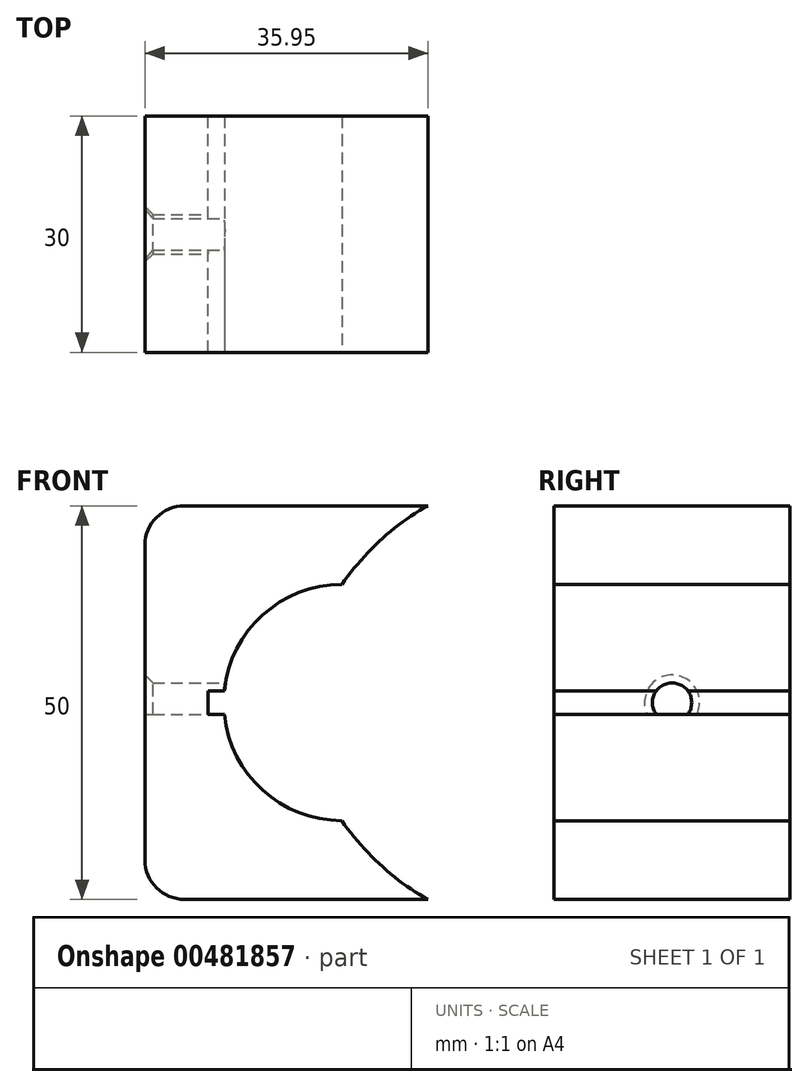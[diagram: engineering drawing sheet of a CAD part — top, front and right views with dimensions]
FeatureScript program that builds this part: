
annotation { "Feature Type Name" : "Feature", "Feature Type Description" : "" }
export const myFeature = defineFeature(function(context is Context, id is Id, definition is map)
    precondition{}
    {
        {
            var Q0;
            Q0=qCreatedBy(makeId("Front.planeOp"),FACE);
            var sketch = newSketch(context, id + "F0", { "sketchPlane" : qUnion([Q0])});
            skLineSegment(sketch, "E0.bottom", {"start": v(-25, 25) * mm, "end": v(25, 25) * mm});
            skLineSegment(sketch, "E0.top", {"start": v(-25, -25) * mm, "end": v(25, -25) * mm});
            skLineSegment(sketch, "E0.left", {"start": v(-25, 25) * mm, "end": v(-25, -25) * mm});
            skLineSegment(sketch, "E0.right", {"start": v(25, 25) * mm, "end": v(25, -25) * mm});
            skPoint(sketch, "E0.middle", {"position": v(0, 0) * mm});
            skCircle(sketch, "E1", {"center": v(0, 0) * mm, "radius": 15 * mm});
            skFitSpline(sketch, "E2", {"points": [v(0, 15) * mm, v(25, 25) * mm, v(25, -25) * mm, v(0, -15) * mm, v(0, 15) * mm]});
            skSolve(sketch);
        }
        {
            var Q0;
            {var subQ4=sQuery(id+"F0.wireOp",EDGE,"E0.left");Q0=makeQuery(id+"F0.imprint","IMPRINT",FACE,{"disambiguationData":[TD([[makeQuery(id+"F0.imprint","IMPRINT",EDGE,{"derivedFrom":subQ4}),1.0]])]});}
            extrude(context, id + "F1", {"entities" : qUnion([Q0]), "oppositeDirection" : true, "depth" : 15 * mm, "hasSecondDirection" : true, "secondDirectionOppositeDirection" : false, "secondDirectionDepth" : 15 * mm});
        }
        {
            var Q0;
            Q0=makeQuery(id+"F1.opExtrude","SWEPT_EDGE",EDGE,{"disambiguationData":[OSD([sQuery(id+"F0.wireOp",EDGE,"E0.bottom"),sQuery(id+"F0.wireOp",EDGE,"E0.left")])]});
            var Q1;
            Q1=makeQuery(id+"F1.opExtrude","SWEPT_EDGE",EDGE,{"disambiguationData":[OSD([sQuery(id+"F0.wireOp",EDGE,"E0.top"),sQuery(id+"F0.wireOp",EDGE,"E0.left")])]});
            fillet(context, id + "F2", {"entities" : qUnion([Q0, Q1]), "radius" : 5 * mm, "tangentPropagation" : true, "allowEdgeOverflow" : false});
        }
        {
            var Q0;
            Q0=qCreatedBy(makeId("Right.planeOp"),FACE);
            var sketch = newSketch(context, id + "F3", { "sketchPlane" : qUnion([Q0])});
            skCircle(sketch, "E3", {"center": v(0, 0) * mm, "radius": 2.5 * mm});
            skLineSegment(sketch, "E4.bottom", {"start": v(-15, 1.5) * mm, "end": v(15, 1.5) * mm});
            skLineSegment(sketch, "E4.top", {"start": v(-15, -1.5) * mm, "end": v(15, -1.5) * mm});
            skLineSegment(sketch, "E4.left", {"start": v(-15, 1.5) * mm, "end": v(-15, -1.5) * mm});
            skLineSegment(sketch, "E4.right", {"start": v(15, 1.5) * mm, "end": v(15, -1.5) * mm});
            skSolve(sketch);
        }
        {
            var Q0;
            {var subQ0=sQuery(id+"F3.wireOp",EDGE,"E4.bottom");var subQ1=sQuery(id+"F3.wireOp",EDGE,"E3");var subQ2=makeQuery(id+"F3.imprint","INTERSECT",VERTEX,{"disambiguationData":[OD(0.0)],"derivedFrom":[subQ1,subQ0]});Q0=makeQuery(id+"F3.imprint","IMPRINT",FACE,{"disambiguationData":[TD([[makeQuery(id+"F3.imprint","IMPRINT",EDGE,{"disambiguationData":[TD([[subQ2,1.0]])],"derivedFrom":subQ1}),1.0]])]});}
            var Q1;
            {var subQ0=sQuery(id+"F3.wireOp",EDGE,"E4.top");var subQ1=sQuery(id+"F3.wireOp",EDGE,"E3");var subQ2=makeQuery(id+"F3.imprint","INTERSECT",VERTEX,{"disambiguationData":[OD(0.0)],"derivedFrom":[subQ1,subQ0]});Q1=makeQuery(id+"F3.imprint","IMPRINT",FACE,{"disambiguationData":[TD([[makeQuery(id+"F3.imprint","IMPRINT",EDGE,{"disambiguationData":[TD([[subQ2,-1.0]])],"derivedFrom":subQ1}),1.0]])]});}
            var Q2;
            {var subQ0=sQuery(id+"F3.wireOp",EDGE,"E4.bottom");var subQ1=sQuery(id+"F3.wireOp",EDGE,"E3");var subQ2=makeQuery(id+"F3.imprint","INTERSECT",VERTEX,{"disambiguationData":[OD(0.0)],"derivedFrom":[subQ1,subQ0]});Q2=makeQuery(id+"F3.imprint","IMPRINT",FACE,{"disambiguationData":[TD([[makeQuery(id+"F3.imprint","IMPRINT",EDGE,{"disambiguationData":[TD([[subQ2,-1.0]])],"derivedFrom":subQ1}),1.0]])]});}
            extrude(context, id + "F4", {"entities" : qUnion([Q0, Q1, Q2]), "operationType" : NewBodyOperationType.REMOVE, "endBound" : BoundingType.THROUGH_ALL, "oppositeDirection" : true, "depth" : 25 * mm});
        }
        {
            var Q0;
            Q0=makeQuery(id+"F4.boolean.opBoolean","INTERSECT",EDGE,{"derivedFrom":[makeQuery(id+"F1.opExtrude","SWEPT_FACE",FACE,{"disambiguationData":[OSD([sQuery(id+"F0.wireOp",EDGE,"E0.left")])]}),makeQuery(id+"F4.opExtrude","SWEPT_FACE",FACE,{"disambiguationData":[OSD([sQuery(id+"F3.wireOp",EDGE,"E3")])]})]});
            chamfer(context, id + "F5", {"entities" : qUnion([Q0]), "width" : 1 * mm, "tangentPropagation" : true});
        }
        {
            var Q0;
            {var subQ5=sQuery(id+"F3.wireOp",EDGE,"E4.right");Q0=makeQuery(id+"F3.imprint","IMPRINT",FACE,{"disambiguationData":[TD([[makeQuery(id+"F3.imprint","IMPRINT",EDGE,{"derivedFrom":subQ5}),-1.0]])]});}
            var Q1;
            {var subQ5=sQuery(id+"F3.wireOp",EDGE,"E4.left");Q1=makeQuery(id+"F3.imprint","IMPRINT",FACE,{"disambiguationData":[TD([[makeQuery(id+"F3.imprint","IMPRINT",EDGE,{"derivedFrom":subQ5}),1.0]])]});}
            extrude(context, id + "F6", {"entities" : qUnion([Q0, Q1]), "operationType" : NewBodyOperationType.REMOVE, "oppositeDirection" : true, "depth" : 17 * mm});
        }
    });
